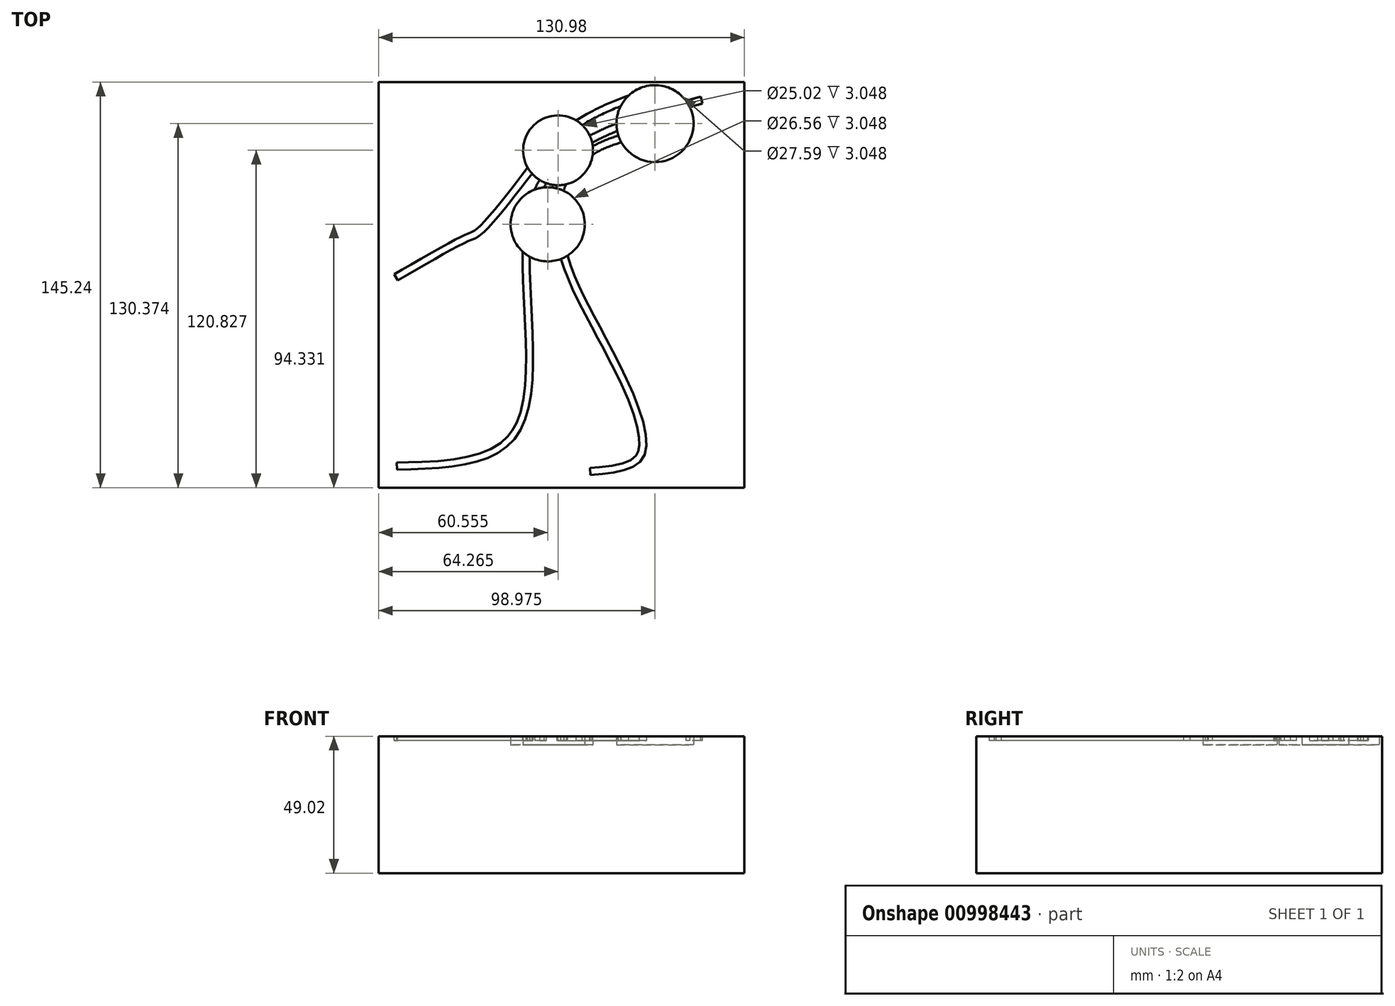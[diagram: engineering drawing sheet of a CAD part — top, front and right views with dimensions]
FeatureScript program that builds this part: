
annotation { "Feature Type Name" : "Feature", "Feature Type Description" : "" }
export const myFeature = defineFeature(function(context is Context, id is Id, definition is map)
    precondition{}
    {
        {
            var Q0;
            Q0=qCreatedBy(makeId("Top.planeOp"),FACE);
            var sketch = newSketch(context, id + "F0", { "sketchPlane" : qUnion([Q0])});
            skLineSegment(sketch, "E0.bottom", {"start": v(65.5, 72.62) * mm, "end": v(-65.5, 72.62) * mm});
            skLineSegment(sketch, "E0.top", {"start": v(65.5, -72.62) * mm, "end": v(-65.5, -72.62) * mm});
            skLineSegment(sketch, "E0.left", {"start": v(65.5, 72.62) * mm, "end": v(65.5, -72.62) * mm});
            skLineSegment(sketch, "E0.right", {"start": v(-65.5, 72.62) * mm, "end": v(-65.5, -72.62) * mm});
            skPoint(sketch, "E0.middle", {"position": v(0, 0) * mm});
            skSolve(sketch);
        }
        {
            var Q0;
            Q0=qSketchRegion(id+"F0",true);
            extrude(context, id + "F1", {"entities" : qUnion([Q0]), "depth" : 49.02 * mm, "offsetDistance" : 25.4 * mm});
        }
        {
            var Q0;
            Q0=makeQuery(id+"F1.opExtrude","CAP_FACE",FACE,{"disambiguationData":[OSD([sQuery(id+"F0.wireOp",EDGE,"E0.bottom"),sQuery(id+"F0.wireOp",EDGE,"E0.top"),sQuery(id+"F0.wireOp",EDGE,"E0.left"),sQuery(id+"F0.wireOp",EDGE,"E0.right")])],"isStart":false});
            var sketch = newSketch(context, id + "F2", { "sketchPlane" : qUnion([Q0])});
            skFitSpline(sketch, "E1", {"points": [v(50.48, 64.98) * mm, v(1.4, 44.56) * mm, v(-11.35, 10.46) * mm, v(-15.66, -53.61) * mm, v(-58.94, -66.17) * mm], "startDerivative": vector(-220.28, -63.03) * mm, "endDerivative": vector(-223.1, -6.27) * mm});
            skFitSpline(sketch, "E2.0", {"points": [v(49.78, 67.42) * mm, v(45.2, 66.11) * mm, v(35.98, 63.48) * mm, v(24.96, 59.88) * mm, v(16.77, 56.63) * mm, v(11.01, 53.96) * mm, v(5.72, 51) * mm, v(1.78, 48.24) * mm, v(-1.06, 45.82) * mm, v(-3.66, 43.26) * mm, v(-6.47, 39.79) * mm, v(-9.16, 35.17) * mm, v(-11.19, 30.1) * mm, v(-12.62, 24.56) * mm, v(-13.51, 18.54) * mm, v(-13.93, 11.99) * mm, v(-13.92, 4.85) * mm, v(-13.62, -2.7) * mm, v(-13.21, -10.48) * mm, v(-12.84, -18.31) * mm, v(-12.67, -25.99) * mm, v(-12.85, -33.31) * mm, v(-13.51, -40.07) * mm, v(-14.8, -46.04) * mm, v(-16.3, -49.75) * mm, v(-17.53, -51.85) * mm, v(-18.41, -53.15) * mm, v(-20.15, -55.22) * mm, v(-23.18, -57.64) * mm, v(-27.68, -59.85) * mm, v(-32.96, -61.42) * mm, v(-38.9, -62.47) * mm, v(-47.44, -63.3) * mm, v(-54.36, -63.5) * mm, v(-59.01, -63.63) * mm]});
            skFitSpline(sketch, "E3", {"points": [v(43.36, 55.24) * mm, v(11.7, 47) * mm, v(0, 30.7) * mm, v(3.83, 5.6) * mm, v(17.32, -21.76) * mm, v(29.68, -60.92) * mm, v(10.38, -68.04) * mm], "startDerivative": vector(-195.84, -28.59) * mm, "endDerivative": vector(-177.68, -14.66) * mm});
            skFitSpline(sketch, "E4", {"points": [v(37.18, 67.6) * mm, v(34, 67.8) * mm, v(6.64, 56.74) * mm, v(-15.28, 33.7) * mm, v(-29.34, 17.58) * mm, v(-32.9, 15.9) * mm, v(-58.56, 1.66) * mm], "startDerivative": vector(-32.27, 8.18) * mm, "endDerivative": vector(-147.14, -85.63) * mm});
            skFitSpline(sketch, "E5.0", {"points": [v(37.8, 70.07) * mm, v(37.63, 70.11) * mm, v(37.23, 70.21) * mm, v(36.44, 70.36) * mm, v(35.5, 70.43) * mm, v(34.42, 70.4) * mm, v(33.18, 70.26) * mm, v(31.3, 69.91) * mm, v(28.5, 69.22) * mm, v(24.52, 67.99) * mm, v(20.14, 66.4) * mm, v(15.52, 64.46) * mm, v(11.65, 62.59) * mm, v(8.63, 60.94) * mm, v(6.43, 59.64) * mm, v(4.32, 58.27) * mm, v(2.33, 56.84) * mm, v(0.44, 55.36) * mm, v(-1.95, 53.33) * mm, v(-4.71, 50.68) * mm, v(-7.74, 47.38) * mm, v(-10.56, 44) * mm, v(-13.25, 40.56) * mm, v(-15.44, 37.67) * mm, v(-17.2, 35.36) * mm, v(-18.99, 33.06) * mm, v(-21.24, 30.2) * mm, v(-23.88, 26.98) * mm, v(-25.95, 24.58) * mm, v(-27.46, 22.9) * mm, v(-28.5, 21.79) * mm, v(-29.45, 20.84) * mm, v(-30.14, 20.2) * mm, v(-30.6, 19.81) * mm, v(-31, 19.5) * mm, v(-31.36, 19.26) * mm, v(-31.72, 19.08) * mm, v(-32.17, 18.9) * mm, v(-32.74, 18.68) * mm, v(-33.32, 18.47) * mm, v(-33.8, 18.27) * mm, v(-34.34, 18.04) * mm, v(-35.1, 17.7) * mm, v(-36.14, 17.2) * mm, v(-37.55, 16.48) * mm, v(-39.62, 15.4) * mm, v(-42.54, 13.8) * mm, v(-46.48, 11.58) * mm, v(-52.17, 8.31) * mm, v(-56.78, 5.64) * mm, v(-59.84, 3.85) * mm]});
            skFitSpline(sketch, "E6.0", {"points": [v(43, 57.75) * mm, v(38.91, 57.16) * mm, v(32.75, 56.26) * mm, v(24.88, 54.65) * mm, v(19.26, 53.13) * mm, v(14.9, 51.5) * mm, v(11.65, 49.93) * mm, v(8.59, 48.13) * mm, v(5.18, 45.48) * mm, v(1.84, 41.73) * mm, v(-0.7, 37.43) * mm, v(-2.07, 33.47) * mm, v(-2.7, 30.12) * mm, v(-2.95, 27.54) * mm, v(-3, 24.92) * mm, v(-2.81, 21.4) * mm, v(-2.18, 16.95) * mm, v(-1.12, 12.55) * mm, v(-0.1, 9.1) * mm, v(0.76, 6.57) * mm, v(1.66, 4.1) * mm, v(2.93, 0.92) * mm, v(4.65, -2.94) * mm, v(6.92, -7.55) * mm, v(9.41, -12.32) * mm, v(11.7, -16.59) * mm, v(13.66, -20.27) * mm, v(15.2, -23.19) * mm, v(16.8, -26.28) * mm, v(19, -30.58) * mm, v(21.7, -36.18) * mm, v(24.56, -42.9) * mm, v(26.39, -48.18) * mm, v(27.35, -52.02) * mm, v(27.78, -54.64) * mm, v(27.9, -56.55) * mm, v(27.82, -57.87) * mm, v(27.7, -58.75) * mm, v(27.5, -59.52) * mm, v(27.26, -60.16) * mm, v(26.95, -60.72) * mm, v(26.45, -61.4) * mm, v(25.63, -62.17) * mm, v(24.27, -63) * mm, v(22.52, -63.69) * mm, v(19.77, -64.44) * mm, v(15.68, -65.06) * mm, v(12.03, -65.36) * mm, v(10.17, -65.5) * mm]});
            skLineSegment(sketch, "E7", {"start": v(-59.84, 3.85) * mm, "end": v(-58.56, 1.66) * mm});
            skLineSegment(sketch, "E8", {"start": v(-59.01, -63.63) * mm, "end": v(-58.94, -66.17) * mm});
            skLineSegment(sketch, "E9", {"start": v(10.17, -65.5) * mm, "end": v(10.38, -68.04) * mm});
            skLineSegment(sketch, "E10", {"start": v(43.36, 55.24) * mm, "end": v(43, 57.75) * mm});
            skLineSegment(sketch, "E11", {"start": v(50.48, 64.98) * mm, "end": v(49.78, 67.42) * mm});
            skLineSegment(sketch, "E12", {"start": v(37.18, 67.6) * mm, "end": v(37.8, 70.07) * mm});
            skSolve(sketch);
        }
        {
            var Q0;
            Q0=makeQuery(id+"F2.imprint","IMPRINT",FACE,{"disambiguationData":[TD([[makeQuery(id+"F2.imprint","IMPRINT",EDGE,{"derivedFrom":sQuery(id+"F2.wireOp",EDGE,"E1")}),-1.0]])]});
            var Q1;
            Q1=makeQuery(id+"F2.imprint","IMPRINT",FACE,{"disambiguationData":[TD([[makeQuery(id+"F2.imprint","IMPRINT",EDGE,{"derivedFrom":sQuery(id+"F2.wireOp",EDGE,"E3")}),-1.0]])]});
            var Q2;
            Q2=makeQuery(id+"F2.imprint","IMPRINT",FACE,{"disambiguationData":[TD([[makeQuery(id+"F2.imprint","IMPRINT",EDGE,{"derivedFrom":sQuery(id+"F2.wireOp",EDGE,"E4")}),-1.0]])]});
            extrude(context, id + "F3", {"entities" : qUnion([Q0, Q1, Q2]), "operationType" : NewBodyOperationType.REMOVE, "oppositeDirection" : true, "depth" : 1.52 * mm, "offsetDistance" : 25.4 * mm});
        }
        {
            var Q0;
            Q0=makeQuery(id+"F5.imprint","IMPRINT",FACE,{"disambiguationData":[TD([[makeQuery(id+"F5.imprint","IMPRINT",EDGE,{"derivedFrom":makeQuery(id+"F1.opExtrude","CAP_EDGE",EDGE,{"disambiguationData":[OSD([sQuery(id+"F0.wireOp",EDGE,"E0.bottom")])],"isStart":false})}),1.0]])]});
            var Q1;
            Q1=makeQuery(id+"F1.opExtrude","CAP_FACE",FACE,{"disambiguationData":[OSD([sQuery(id+"F0.wireOp",EDGE,"E0.bottom"),sQuery(id+"F0.wireOp",EDGE,"E0.top"),sQuery(id+"F0.wireOp",EDGE,"E0.left"),sQuery(id+"F0.wireOp",EDGE,"E0.right")])],"isStart":false});
            cPlane(context, id + "F4", {"entities" : qUnion([Q0, Q1]), "cplaneType" : CPlaneType.OFFSET, "offset" : 3.05 * mm, "oppositeDirection" : true, "width" : 152.4 * mm, "height" : 152.4 * mm});
        }
        {
            var Q0;
            Q0=qCreatedBy(id+"F4.planeOp",FACE);
            var sketch = newSketch(context, id + "F5", { "sketchPlane" : qUnion([Q0])});
            skCircle(sketch, "E13", {"center": v(-1.23, 48.2) * mm, "radius": 12.51 * mm});
            skCircle(sketch, "E14", {"center": v(-4.93, 21.71) * mm, "radius": 13.28 * mm});
            skCircle(sketch, "E15", {"center": v(33.49, 57.75) * mm, "radius": 13.8 * mm});
            skSolve(sketch);
        }
        {
            var Q0;
            Q0 = qSketchRegion(id + "F5", true);
            extrude(context, id + "F6", {"entities" : qUnion([Q0]), "operationType" : NewBodyOperationType.REMOVE, "endBound" : BoundingType.THROUGH_ALL, "depth" : 25.4 * mm, "offsetDistance" : 25.4 * mm});
        }
    });
